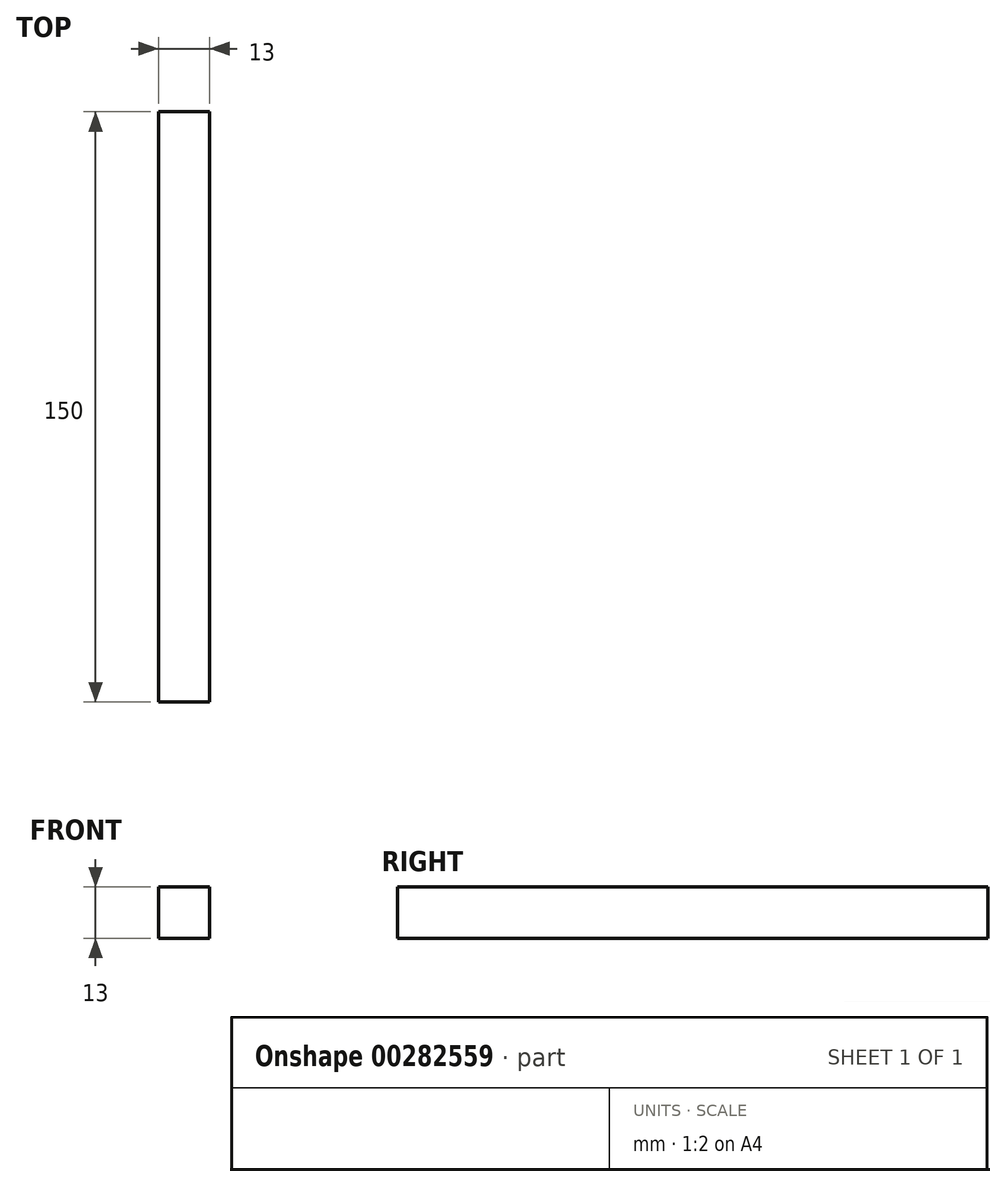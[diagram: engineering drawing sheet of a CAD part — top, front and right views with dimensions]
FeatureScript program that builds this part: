
annotation { "Feature Type Name" : "Feature", "Feature Type Description" : "" }
export const myFeature = defineFeature(function(context is Context, id is Id, definition is map)
    precondition{}
    {
        {
            var Q0;
            Q0=qCreatedBy(makeId("Front.planeOp"),FACE);
            var sketch = newSketch(context, id + "F0", { "sketchPlane" : qUnion([Q0])});
            skLineSegment(sketch, "E0.bottom", {"start": v(6.5, -6.5) * mm, "end": v(-6.5, -6.5) * mm});
            skLineSegment(sketch, "E0.top", {"start": v(6.5, 6.5) * mm, "end": v(-6.5, 6.5) * mm});
            skLineSegment(sketch, "E0.left", {"start": v(6.5, -6.5) * mm, "end": v(6.5, 6.5) * mm});
            skLineSegment(sketch, "E0.right", {"start": v(-6.5, -6.5) * mm, "end": v(-6.5, 6.5) * mm});
            skPoint(sketch, "E0.middle", {"position": v(0, 0) * mm});
            skSolve(sketch);
        }
        {
            var Q0;
            Q0=makeQuery(id+"F0.imprint","IMPRINT",FACE,{"disambiguationData":[TD([[makeQuery(id+"F0.imprint","IMPRINT",EDGE,{"derivedFrom":sQuery(id+"F0.wireOp",EDGE,"E0.bottom")}),-1.0]])]});
            extrude(context, id + "F1", {"entities" : qUnion([Q0]), "depth" : 150 * mm});
        }
    });
